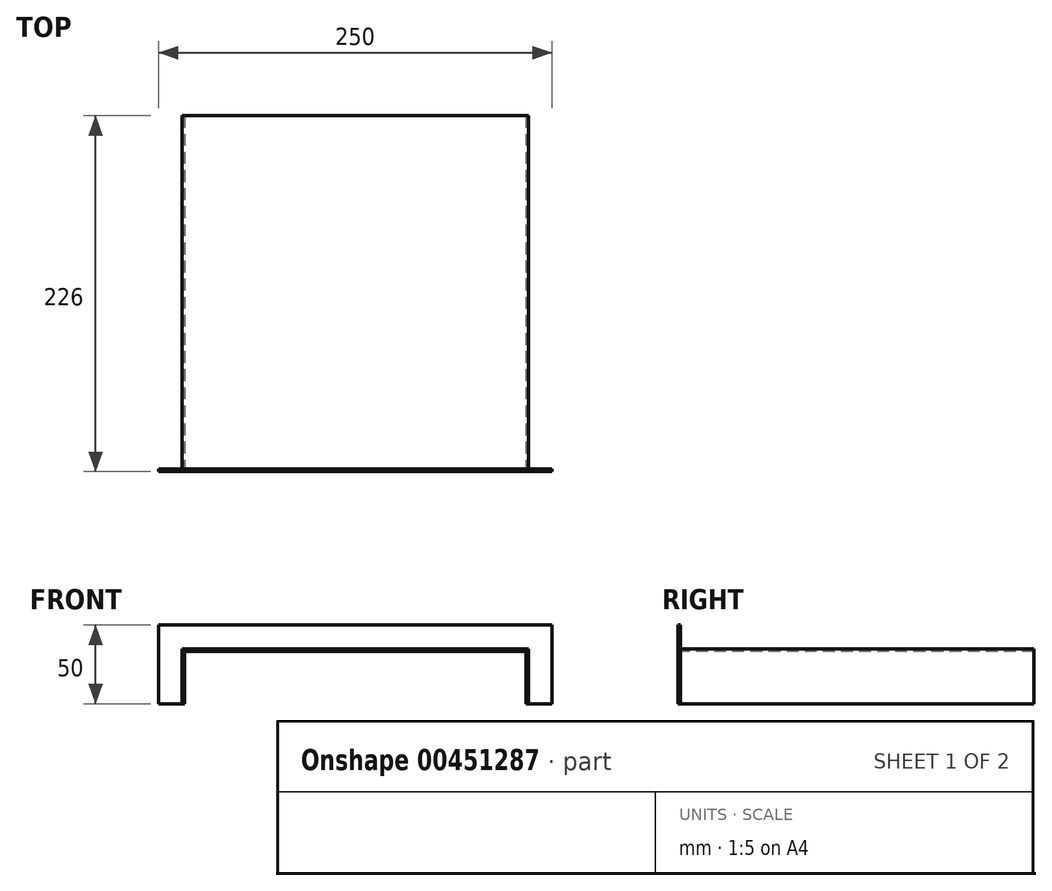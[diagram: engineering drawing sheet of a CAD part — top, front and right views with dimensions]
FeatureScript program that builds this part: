
annotation { "Feature Type Name" : "Feature", "Feature Type Description" : "" }
export const myFeature = defineFeature(function(context is Context, id is Id, definition is map)
    precondition{}
    {
        {
            var Q0;
            Q0=qCreatedBy(makeId("Front.planeOp"),FACE);
            var sketch = newSketch(context, id + "F0", { "sketchPlane" : qUnion([Q0])});
            skLineSegment(sketch, "E0", {"start": v(-325.33, 62.1) * mm, "end": v(-325.33, 12.1) * mm});
            skLineSegment(sketch, "E1", {"start": v(-323.73, 43.9) * mm, "end": v(-323.73, 12.1) * mm});
            skArc(sketch, "E2", {"start": v(-322.13, 45.5) * mm, "mid": v(-323.26, 45.03) * mm, "end": v(-323.73, 43.9) * mm});
            skLineSegment(sketch, "E3", {"start": v(-340.33, 62.1) * mm, "end": v(-340.33, 12.1) * mm});
            skLineSegment(sketch, "E4", {"start": v(-105.33, 62.1) * mm, "end": v(-105.33, 12.1) * mm});
            skLineSegment(sketch, "E5", {"start": v(-106.93, 43.9) * mm, "end": v(-106.93, 12.1) * mm});
            skLineSegment(sketch, "E6", {"start": v(-90.33, 62.1) * mm, "end": v(-90.33, 12.1) * mm});
            skLineSegment(sketch, "E7", {"start": v(-105.33, 12.1) * mm, "end": v(-106.93, 12.1) * mm});
            skLineSegment(sketch, "E8", {"start": v(-323.73, 12.1) * mm, "end": v(-325.33, 12.1) * mm});
            skLineSegment(sketch, "E9", {"start": v(-105.33, 47.1) * mm, "end": v(-325.33, 47.1) * mm});
            skLineSegment(sketch, "E10", {"start": v(-105.33, 45.5) * mm, "end": v(-325.33, 45.5) * mm});
            skArc(sketch, "E11", {"start": v(-105.33, 43.9) * mm, "mid": v(-105.44, 44.72) * mm, "end": v(-105.76, 45.5) * mm});
            skArc(sketch, "E12", {"start": v(-105.76, 45.5) * mm, "mid": v(-106.93, 46.67) * mm, "end": v(-108.53, 47.1) * mm});
            skLineSegment(sketch, "E13", {"start": v(-108.53, 45.5) * mm, "end": v(-322.13, 45.5) * mm});
            skArc(sketch, "E14", {"start": v(-106.93, 43.9) * mm, "mid": v(-107.4, 45.03) * mm, "end": v(-108.53, 45.5) * mm});
            skLineSegment(sketch, "E15", {"start": v(-90.33, 62.1) * mm, "end": v(-340.33, 62.1) * mm});
            skLineSegment(sketch, "E16", {"start": v(-105.33, 12.1) * mm, "end": v(-90.33, 12.1) * mm});
            skLineSegment(sketch, "E17", {"start": v(-325.33, 12.1) * mm, "end": v(-340.33, 12.1) * mm});
            skLineSegment(sketch, "E18", {"start": v(21.57, 12.1) * mm, "end": v(247.57, 12.1) * mm});
            skLineSegment(sketch, "E19", {"start": v(247.57, 12.1) * mm, "end": v(247.57, 47.1) * mm});
            skLineSegment(sketch, "E20", {"start": v(24.77, 47.1) * mm, "end": v(244.37, 47.1) * mm});
            skLineSegment(sketch, "E21", {"start": v(24.77, 45.5) * mm, "end": v(244.37, 45.5) * mm});
            skLineSegment(sketch, "E22", {"start": v(21.57, 62.1) * mm, "end": v(23.17, 62.1) * mm});
            skLineSegment(sketch, "E23", {"start": v(245.97, 62.1) * mm, "end": v(247.57, 62.1) * mm});
            skLineSegment(sketch, "E24", {"start": v(247.57, 12.1) * mm, "end": v(247.57, 62.1) * mm});
            skLineSegment(sketch, "E25", {"start": v(245.97, 12.1) * mm, "end": v(245.97, 62.1) * mm});
            skLineSegment(sketch, "E26", {"start": v(21.57, 12.1) * mm, "end": v(21.57, 62.1) * mm});
            skArc(sketch, "E27", {"start": v(21.57, 48.7) * mm, "mid": v(22.5, 46.43) * mm, "end": v(24.77, 45.5) * mm});
            skLineSegment(sketch, "E28", {"start": v(23.17, 12.1) * mm, "end": v(23.17, 62.1) * mm});
            skArc(sketch, "E29", {"start": v(23.17, 48.7) * mm, "mid": v(23.63, 47.56) * mm, "end": v(24.77, 47.1) * mm});
            skLineSegment(sketch, "E30", {"start": v(21.57, 12.1) * mm, "end": v(23.17, 12.1) * mm});
            skLineSegment(sketch, "E31", {"start": v(245.97, 12.1) * mm, "end": v(247.57, 12.1) * mm});
            skLineSegment(sketch, "E32", {"start": v(-105.33, 143.29) * mm, "end": v(-325.33, 143.29) * mm});
            skLineSegment(sketch, "E33", {"start": v(-105.33, 369.29) * mm, "end": v(-325.33, 369.29) * mm});
            skLineSegment(sketch, "E34", {"start": v(-105.33, 367.69) * mm, "end": v(-105.33, 144.89) * mm});
            skLineSegment(sketch, "E35", {"start": v(-325.33, 367.69) * mm, "end": v(-325.33, 144.89) * mm});
            skLineSegment(sketch, "E36", {"start": v(-90.33, 369.29) * mm, "end": v(-90.33, 367.69) * mm});
            skLineSegment(sketch, "E37", {"start": v(-90.33, 144.89) * mm, "end": v(-90.33, 143.29) * mm});
            skLineSegment(sketch, "E38", {"start": v(-340.33, 369.29) * mm, "end": v(-340.33, 367.69) * mm});
            skLineSegment(sketch, "E39", {"start": v(-340.33, 144.89) * mm, "end": v(-340.33, 143.29) * mm});
            skLineSegment(sketch, "E40", {"start": v(-90.33, 143.29) * mm, "end": v(-340.33, 143.29) * mm});
            skLineSegment(sketch, "E41", {"start": v(-90.33, 144.89) * mm, "end": v(-340.33, 144.89) * mm});
            skLineSegment(sketch, "E42", {"start": v(-90.33, 367.69) * mm, "end": v(-340.33, 367.69) * mm});
            skLineSegment(sketch, "E43", {"start": v(-90.33, 369.29) * mm, "end": v(-340.33, 369.29) * mm});
            skLineSegment(sketch, "E44", {"start": v(-106.93, 367.69) * mm, "end": v(-106.93, 144.89) * mm});
            skLineSegment(sketch, "E45", {"start": v(-323.73, 367.69) * mm, "end": v(-323.73, 144.89) * mm});
            skArc(sketch, "E46", {"start": v(-322.13, 47.1) * mm, "mid": v(-323.73, 46.67) * mm, "end": v(-324.9, 45.5) * mm});
            skArc(sketch, "E47", {"start": v(-324.9, 45.5) * mm, "mid": v(-325.22, 44.72) * mm, "end": v(-325.33, 43.9) * mm});
            skArc(sketch, "E48", {"start": v(244.37, 45.5) * mm, "mid": v(246.63, 46.43) * mm, "end": v(247.57, 48.7) * mm});
            skArc(sketch, "E49", {"start": v(244.37, 47.1) * mm, "mid": v(245.5, 47.56) * mm, "end": v(245.97, 48.7) * mm});
            skSolve(sketch);
        }
        {
            var Q0;
            {var subQ3=sQuery(id+"F0.wireOp",EDGE,"E15");var subQ4=sQuery(id+"F0.wireOp",EDGE,"E0");var subQ5=makeQuery(id+"F0.imprint","INTERSECT",VERTEX,{"derivedFrom":[subQ4,subQ3]});Q0=makeQuery(id+"F0.imprint","IMPRINT",FACE,{"disambiguationData":[TD([[makeQuery(id+"F0.imprint","IMPRINT",EDGE,{"disambiguationData":[TD([[subQ5,-1.0]])],"derivedFrom":subQ4}),1.0]])]});}
            var Q1;
            {var subQ7=sQuery(id+"F0.wireOp",EDGE,"E6");Q1=makeQuery(id+"F0.imprint","IMPRINT",FACE,{"disambiguationData":[TD([[makeQuery(id+"F0.imprint","IMPRINT",EDGE,{"derivedFrom":subQ7}),-1.0]])]});}
            var Q2;
            {var subQ7=sQuery(id+"F0.wireOp",EDGE,"E3");Q2=makeQuery(id+"F0.imprint","IMPRINT",FACE,{"disambiguationData":[TD([[makeQuery(id+"F0.imprint","IMPRINT",EDGE,{"derivedFrom":subQ7}),1.0]])]});}
            extrude(context, id + "F1", {"entities" : qUnion([Q0, Q1, Q2]), "oppositeDirection" : true, "depth" : 1.6 * mm});
        }
        {
            var Q0;
            Q0=makeQuery(id+"F0.imprint","IMPRINT",FACE,{"disambiguationData":[TD([[makeQuery(id+"F0.imprint","IMPRINT",EDGE,{"derivedFrom":sQuery(id+"F0.wireOp",EDGE,"E5")}),1.0]])]});
            var Q1;
            {var subQ0=sQuery(id+"F0.wireOp",EDGE,"E12");Q1=makeQuery(id+"F0.imprint","IMPRINT",FACE,{"disambiguationData":[TD([[makeQuery(id+"F0.imprint","IMPRINT",EDGE,{"derivedFrom":subQ0}),1.0]])]});}
            var Q2;
            Q2=makeQuery(id+"F0.imprint","IMPRINT",FACE,{"disambiguationData":[TD([[makeQuery(id+"F0.imprint","IMPRINT",EDGE,{"derivedFrom":sQuery(id+"F0.wireOp",EDGE,"E1")}),-1.0]])]});
            extrude(context, id + "F2", {"entities" : qUnion([Q0, Q1, Q2]), "oppositeDirection" : true, "depth" : 226 * mm});
        }
    });
